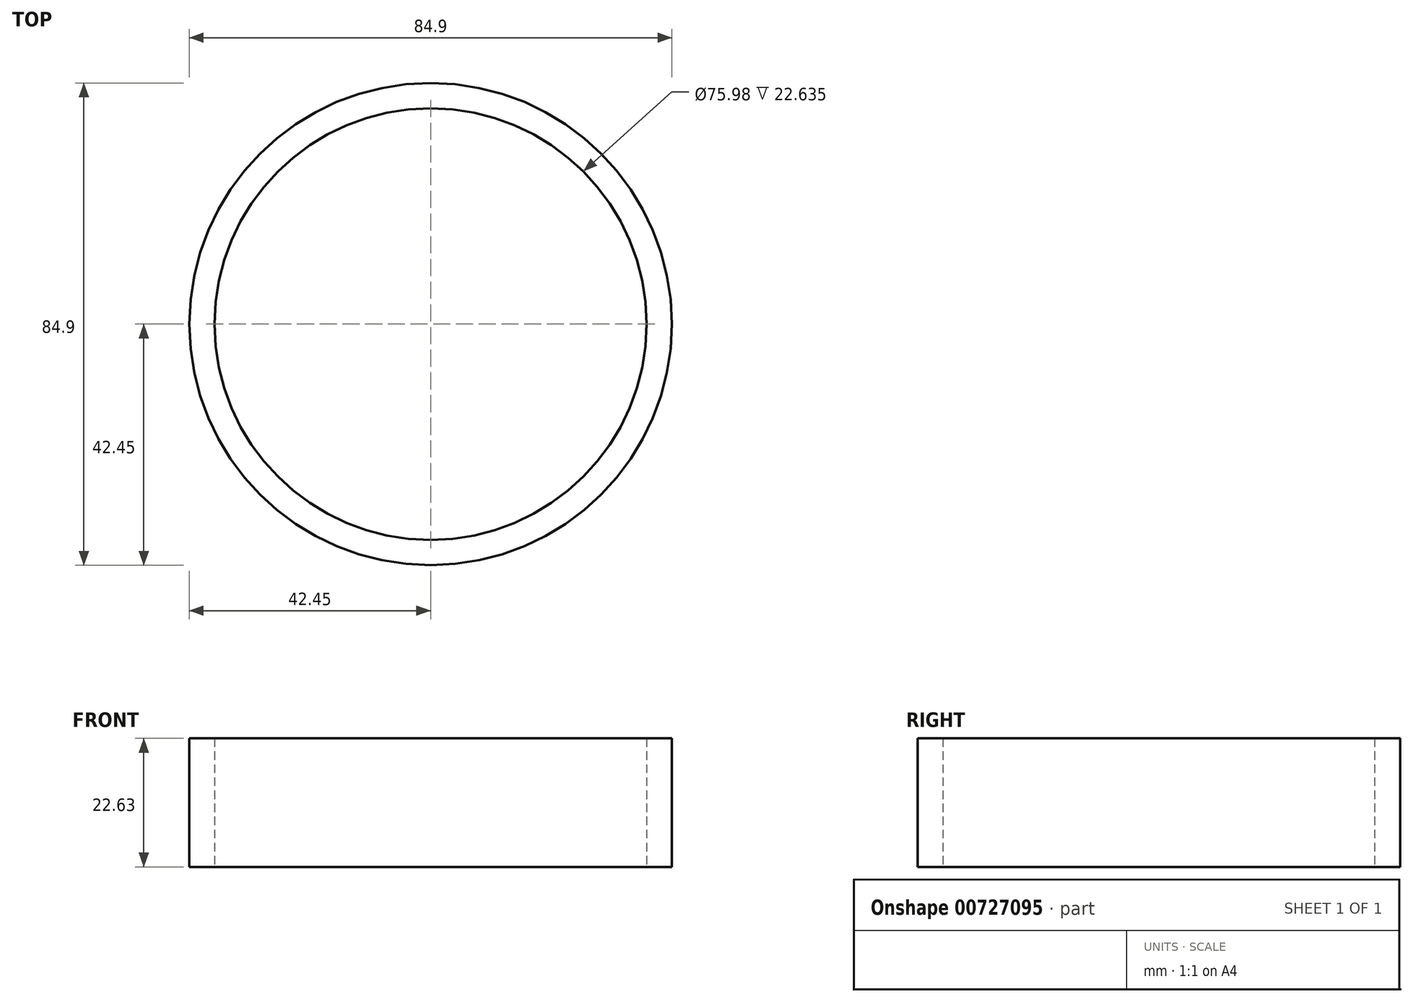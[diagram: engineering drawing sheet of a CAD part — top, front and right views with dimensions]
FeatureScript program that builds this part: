
annotation { "Feature Type Name" : "Feature", "Feature Type Description" : "" }
export const myFeature = defineFeature(function(context is Context, id is Id, definition is map)
    precondition{}
    {
        {
            var Q0;
            Q0=qCreatedBy(makeId("Top.planeOp"),FACE);
            var sketch = newSketch(context, id + "F0", { "sketchPlane" : qUnion([Q0])});
            skCircle(sketch, "E0", {"center": v(0, 0) * mm, "radius": 42.45 * mm});
            skCircle(sketch, "E1", {"center": v(0, 0) * mm, "radius": 37.99 * mm});
            skSolve(sketch);
        }
        {
            var Q0;
            Q0=makeQuery(id+"F0.imprint","IMPRINT",FACE,{"disambiguationData":[TD([[makeQuery(id+"F0.imprint","IMPRINT",EDGE,{"derivedFrom":sQuery(id+"F0.wireOp",EDGE,"E0")}),1.0]])]});
            var Q1;
            Q1 = qSketchRegion(id + "F0", true);
            extrude(context, id + "F1", {"entities" : qUnion([Q0, Q1]), "depth" : 22.63 * mm, "offsetDistance" : 25.4 * mm});
        }
    });
